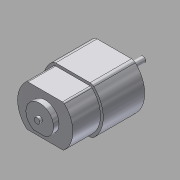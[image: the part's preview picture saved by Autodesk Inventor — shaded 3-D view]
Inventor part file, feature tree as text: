
AUTODESK INVENTOR PART (.ipt)
format: ipt  version: 2015 (Build 190159000, 159)  size: 139,776 bytes
history: native  units: in
note: dims shown in document units (in); Inventor stores cm internally (conversion verified against a paired STEP export)
features: sketch x5, other x3
ambient origin geometry x8: Origin, YZ Plane, XZ Plane, XY Plane, X Axis, Y Axis, Z Axis, Center Point
bodies: Solid1 (feature_tree)
feature tree (8):
  other  "motor_MIR4.ipt"
  other  "Solid1::motor_MIR4.ipt"
  other  "TaggingFeature1"
  sketch  "Sketch1"  dims[d0=0.3937in]
  sketch  "Sketch2"
  sketch  "Sketch3"
  sketch  "Sketch4"
  sketch  "Sketch5"
